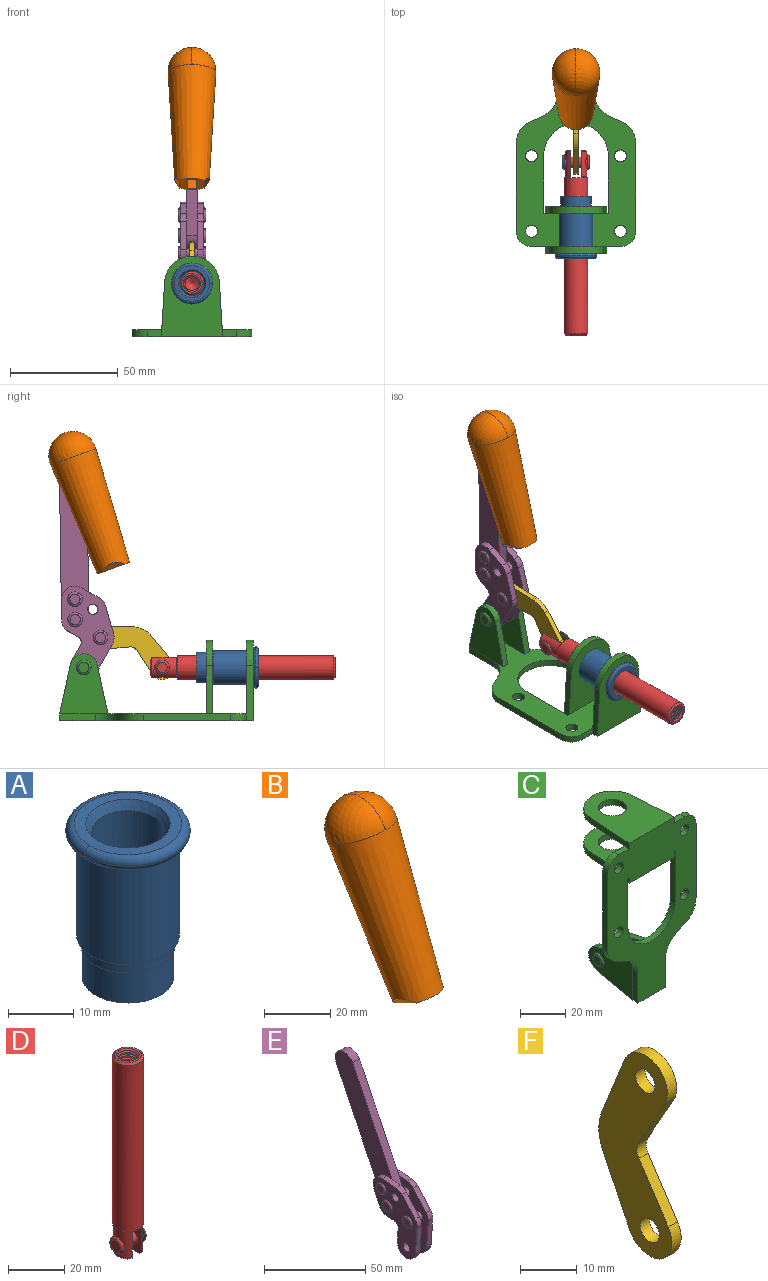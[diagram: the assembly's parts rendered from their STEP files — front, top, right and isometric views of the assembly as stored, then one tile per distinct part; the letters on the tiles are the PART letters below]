
ASSEMBLY  parts=6 mates=6
PART A: 15 faces, bbox 20.6x20.6x28.7 mm
  f0: torus R=8.26mm, axis (0,0,1), area 56.8mm2, adj f1,f10,f12
  f1: torus R=8.26mm, axis (0,0,1), area 56.8mm2, adj f0,f6,f13
  f2: cylinder r=5.59mm len=25.91mm, axis (0,0,1), area 909.6mm2, adj f3,f4
  f3: cone r=6.86mm half-angle=45deg, axis (0,0,-1), area 70.2mm2, adj f2,f14
  f4: cone r=6.47mm half-angle=30deg, axis (0,0,1), area 66.7mm2, adj f2,f13
  f5: cylinder r=7.04mm len=14.07mm, axis (0,0,1), area 252.6mm2, adj f11,f14
  f6: torus R=8.26mm, axis (0,0,1), area 56.8mm2, adj f1,f12,f13
  f7: cylinder r=7.16mm len=14.33mm, axis (0,0,1), area 91.5mm2, adj f9,f11
  f8: cylinder r=7.86mm len=18.42mm, axis (0,0,1), area 909.6mm2, adj f9,f10
  f9: plane 15.72x15.72mm, normal (0,0,-1), area 33mm2, adj f7,f8
  f10: plane 16.51x16.51mm, normal (0,0,-1), area 19.9mm2, adj f0,f8,f12
  f11: plane 14.33x14.33mm, normal (0,0,-1), area 5.7mm2, adj f5,f7
  f12: torus R=8.26mm, axis (0,0,1), area 56.8mm2, adj f0,f6,f10
  f13: plane 16.51x16.51mm, normal (0,0,1), area 82.7mm2, adj f1,f4,f6
  f14: plane 14.07x14.07mm, normal (0,0,-1), area 7.8mm2, adj f3,f5
PART B: 11 faces, bbox 22.3x42.6x64.5 mm
  f0: sphere r=11.13mm, area 411.4mm2, adj f1,f8
  f1: cone r=11.11mm half-angle=3.3deg, axis (0,0.44,0.9), area 3251.8mm2, adj f0,f7,f8,f9,f10
  f2: cylinder r=6.16mm len=11.7mm, axis (1,0,0), area 89.5mm2, adj f3,f4,f5,f6
  f3: plane 60.23x36.75mm, normal (-1,0,0), area 763.6mm2, adj f2,f4,f6,f10
  f4: plane 51.37x25.05mm, normal (0,0.9,-0.44), area 264.2mm2, adj f2,f3,f5,f10
  f5: plane 60.23x36.75mm, normal (1,0,0), area 763.6mm2, adj f2,f4,f6,f10
  f6: plane 51.37x25.05mm, normal (0,-0.9,0.44), area 264.2mm2, adj f2,f3,f5,f10
  f7: plane 9.95x5.95mm, normal (0.71,-0.31,-0.64), area 25.8mm2, adj f1,f10
  f8: sphere r=11.13mm, area 411.4mm2, adj f0,f1
  f9: plane 9.95x5.95mm, normal (-0.71,-0.31,-0.64), area 25.8mm2, adj f1,f10
  f10: plane 14.27x11.38mm, normal (0,-0.44,-0.9), area 106.7mm2, adj f1,f3,f4,f5,f6,f7,f9
PART C: 55 faces, bbox 55.7x37.4x89.8 mm
  f0: torus R=2.41mm, axis (-1,0,0), area 15mm2, adj f11,f15,f25
  f1: torus R=2.41mm, axis (-1,0,0), area 15mm2, adj f10,f12,f22
  f2: cylinder r=2.78mm len=5.56mm, axis (0,-1,0), area 54.2mm2, adj f30,f54
  f3: cylinder r=14.99mm len=29.97mm, axis (0,-1,0), area 145.9mm2, adj f30,f49,f53,f54
  f4: cylinder r=2.78mm len=5.56mm, axis (0,-1,0), area 54.2mm2, adj f30,f54
  f5: cylinder r=2.78mm len=5.56mm, axis (0,-1,0), area 54.2mm2, adj f30,f54
  f6: cylinder r=2.78mm len=5.56mm, axis (0,-1,0), area 54.2mm2, adj f30,f54
  f7: cylinder r=6.35mm len=12.7mm, axis (0,0,1), area 123.6mm2, adj f27,f51
  f8: cylinder r=6.35mm len=12.7mm, axis (0,0,-1), area 124.7mm2, adj f21,f35
  f9: cylinder r=2.41mm len=11.18mm, axis (-1,0,0), area 169.4mm2, adj f16,f19
  f10: plane 4.83x4.83mm, normal (1,0,0), area 18.3mm2, adj f1,f12
  f11: plane 4.83x4.83mm, normal (-1,0,0), area 18.3mm2, adj f0,f15
  f12: torus R=2.41mm, axis (-1,0,0), area 15mm2, adj f1,f10,f22
  f13: cylinder r=6.35mm len=12.41mm, axis (1,0,0), area 53.4mm2, adj f18,f19,f22,f23
  f14: cylinder r=6.35mm len=12.41mm, axis (-1,0,0), area 53.4mm2, adj f16,f17,f24,f25
  f15: torus R=2.41mm, axis (-1,0,0), area 15mm2, adj f0,f11,f25
  f16: plane 27.86x22.35mm, normal (1,0,0), area 425.4mm2, adj f9,f14,f17,f24,f30
  f17: plane 22.86x4.97mm, normal (0,0.21,0.98), area 72.5mm2, adj f14,f16,f25,f30
  f18: plane 22.86x4.97mm, normal (0,0.21,0.98), area 72.5mm2, adj f13,f19,f22,f30
  f19: plane 27.86x22.35mm, normal (-1,0,0), area 425.4mm2, adj f9,f13,f18,f23,f30
  f20: cylinder r=12.7mm len=25.35mm, axis (0,0,-1), area 119.8mm2, adj f21,f34,f35,f36
  f21: plane 34.21x28.07mm, normal (0,0,-1), area 702.4mm2, adj f8,f20,f30,f34,f36
  f22: plane 27.96x22.45mm, normal (1,0,0), area 407.2mm2, adj f1,f12,f13,f18,f23,f30,f42,f43
  f23: plane 22.86x4.97mm, normal (0,0.21,-0.98), area 72.5mm2, adj f13,f19,f22,f44
  f24: plane 22.86x4.97mm, normal (0,0.21,-0.98), area 72.5mm2, adj f14,f16,f25,f44
  f25: plane 27.86x22.35mm, normal (-1,0,0), area 407.1mm2, adj f0,f14,f15,f17,f24,f30,f45,f46
  f26: plane 3.1x0.95mm, normal (0,0,-1), area 2.7mm2, adj f30,f49,f50,f54
  f27: plane 34.21x28.07mm, normal (0,0,1), area 702.4mm2, adj f7,f28,f30,f50,f52
  f28: cylinder r=12.7mm len=25.35mm, axis (0,0,1), area 118.8mm2, adj f27,f50,f51,f52
  f29: plane 3.1x0.95mm, normal (0,0,-1), area 2.7mm2, adj f30,f52,f53,f54
  f30: plane 86.54x55.63mm, normal (0,1,0), area 2362.9mm2, adj f2,f3,f4,f5,f6,f16,f17,f18
  f31: plane 40.56x3.1mm, normal (-1,0,0), area 125.7mm2, adj f30,f32,f48,f54
  f32: cylinder r=7.11mm len=7.11mm, axis (0,-1,0), area 34.6mm2, adj f30,f31,f33,f54
  f33: plane 6.67x3.1mm, normal (0,0,1), area 20.4mm2, adj f30,f32,f34,f54
  f34: plane 25.39x3.13mm, normal (-1,0.06,0), area 79.5mm2, adj f20,f21,f33,f35,f54
  f35: plane 37.31x28.45mm, normal (0,0,1), area 789.9mm2, adj f8,f20,f34,f36,f54
  f36: plane 25.39x3.13mm, normal (1,0.06,0), area 79.5mm2, adj f20,f21,f35,f37,f54
  f37: plane 6.67x3.1mm, normal (0,0,1), area 20.4mm2, adj f30,f36,f38,f54
  f38: cylinder r=7.11mm len=7.11mm, axis (0,-1,0), area 34.6mm2, adj f30,f37,f39,f54
  f39: plane 40.56x3.1mm, normal (1,0,0), area 125.7mm2, adj f30,f38,f40,f54
  f40: cylinder r=11.18mm len=10.16mm, axis (0,-1,0), area 39.5mm2, adj f30,f39,f41,f54
  f41: plane 6.09x3.1mm, normal (0.42,0,-0.91), area 20.8mm2, adj f30,f40,f42,f54
  f42: cylinder r=11.18mm len=9.41mm, axis (0,-1,0), area 37.2mm2, adj f22,f30,f41,f43,f54
  f43: plane 16.5x3.1mm, normal (1,0,0), area 51.1mm2, adj f22,f42,f44,f54
  f44: plane 17.37x3.1mm, normal (0,0,-1), area 53.8mm2, adj f23,f24,f30,f43,f45,f54
  f45: plane 16.5x3.1mm, normal (-1,0,0), area 51.1mm2, adj f25,f44,f46,f54
  f46: cylinder r=11.18mm len=9.41mm, axis (0,-1,0), area 37.2mm2, adj f25,f30,f45,f47,f54
  f47: plane 6.09x3.1mm, normal (-0.42,0,-0.91), area 20.8mm2, adj f30,f46,f48,f54
  f48: cylinder r=11.18mm len=10.16mm, axis (0,-1,0), area 39.5mm2, adj f30,f31,f47,f54
  f49: plane 26.54x3.1mm, normal (-1,0,0), area 82.3mm2, adj f3,f26,f30,f54
  f50: plane 25.39x3.1mm, normal (1,0.06,0), area 78.8mm2, adj f26,f27,f28,f51,f54
  f51: plane 37.31x28.45mm, normal (0,0,-1), area 789.9mm2, adj f7,f28,f50,f52,f54
  f52: plane 25.39x3.1mm, normal (-1,0.06,0), area 78.8mm2, adj f27,f28,f29,f51,f54
  f53: plane 26.54x3.1mm, normal (1,0,0), area 82.3mm2, adj f3,f29,f30,f54
  f54: plane 89.66x55.63mm, normal (0,-1,0), area 2678.5mm2, adj f2,f3,f4,f5,f6,f26,f29,f31
PART D: 48 faces, bbox 12.6x11.1x86.1 mm
  f0: torus R=2.41mm, axis (-1,0,0), area 15mm2, adj f30,f32,f34
  f1: torus R=2.41mm, axis (-1,0,0), area 15mm2, adj f29,f31,f33
  f2: cylinder r=5.54mm len=72.39mm, axis (0,0,1), area 2518.5mm2, adj f3,f4,f42,f43
  f3: cone r=5.54mm half-angle=45deg, axis (0,0,1), area 7.6mm2, adj f2,f5,f41
  f4: cone r=5.54mm half-angle=45deg, axis (0,0,-1), area 34.9mm2, adj f2,f39
  f5: cylinder r=5.08mm len=11.48mm, axis (0,0,1), area 108.3mm2, adj f3,f7,f8,f41
  f6: cylinder r=2.41mm len=4.83mm, axis (-1,0,0), area 71.2mm2, adj f40,f41
  f7: cylinder r=2.41mm len=4.83mm, axis (-1,0,0), area 7.6mm2, adj f5,f34
  f8: cone r=5.08mm half-angle=45deg, axis (0,0,1), area 10.6mm2, adj f5,f37,f41
  f9: cone r=3.98mm half-angle=45deg, axis (0,0,1), area 17.6mm2, adj f27,f39,f45,f46,f47
  f10: cylinder r=2.41mm len=4.83mm, axis (-1,0,0), area 7.6mm2, adj f33,f38
  f11: cylinder r=3.2mm len=6.4mm, axis (0,0,1), area 78.4mm2, adj f12,f28,f44,f45,f47
  f12: cylinder r=3.2mm len=6.4mm, axis (0,0,1), area 10.5mm2, adj f11,f13,f45,f47
  f13: cylinder r=3.2mm len=6.4mm, axis (0,0,1), area 10.5mm2, adj f12,f14,f45,f47
  f14: cylinder r=3.2mm len=6.4mm, axis (0,0,1), area 10.5mm2, adj f13,f15,f45,f47
  f15: cylinder r=3.2mm len=6.4mm, axis (0,0,1), area 10.5mm2, adj f14,f16,f45,f47
  f16: cylinder r=3.2mm len=6.4mm, axis (0,0,1), area 10.5mm2, adj f15,f17,f45,f47
  f17: cylinder r=3.2mm len=6.4mm, axis (0,0,1), area 10.5mm2, adj f16,f18,f45,f47
  f18: cylinder r=3.2mm len=6.4mm, axis (0,0,1), area 10.5mm2, adj f17,f19,f45,f47
  f19: cylinder r=3.2mm len=6.4mm, axis (0,0,1), area 10.5mm2, adj f18,f20,f45,f47
  f20: cylinder r=3.2mm len=6.4mm, axis (0,0,1), area 10.5mm2, adj f19,f21,f45,f47
  f21: cylinder r=3.2mm len=6.4mm, axis (0,0,1), area 10.5mm2, adj f20,f22,f45,f47
  f22: cylinder r=3.2mm len=6.4mm, axis (0,0,1), area 10.5mm2, adj f21,f23,f45,f47
  f23: cylinder r=3.2mm len=6.4mm, axis (0,0,1), area 10.5mm2, adj f22,f24,f45,f47
  f24: cylinder r=3.2mm len=6.4mm, axis (0,0,1), area 10.5mm2, adj f23,f25,f45,f47
  f25: cylinder r=3.2mm len=6.4mm, axis (0,0,1), area 10.5mm2, adj f24,f26,f45,f47
  f26: cylinder r=3.2mm len=6.4mm, axis (0,0,1), area 10.5mm2, adj f25,f27,f45,f47
  f27: cylinder r=3.2mm len=6.4mm, axis (0,0,1), area 7.4mm2, adj f9,f26,f45,f47
  f28: cone r=3.2mm half-angle=60deg, axis (0,0,1), area 37.2mm2, adj f11
  f29: plane 4.83x4.83mm, normal (-1,0,0), area 18.3mm2, adj f1,f31
  f30: plane 4.83x4.83mm, normal (1,0,0), area 18.3mm2, adj f0,f32
  f31: torus R=2.41mm, axis (-1,0,0), area 15mm2, adj f1,f29,f33
  f32: torus R=2.41mm, axis (-1,0,0), area 15mm2, adj f0,f30,f34
  f33: plane 6.83x6.83mm, normal (1,0,0), area 18.3mm2, adj f1,f10,f31
  f34: plane 6.83x6.83mm, normal (-1,0,0), area 18.3mm2, adj f0,f7,f32
  f35: cone r=5.08mm half-angle=45deg, axis (0,0,1), area 10.6mm2, adj f36,f38,f40
  f36: plane 7.25x1.97mm, normal (0,0,-1), area 10mm2, adj f35,f40
  f37: plane 7.25x1.97mm, normal (0,0,-1), area 10mm2, adj f8,f41
  f38: cylinder r=5.08mm len=11.48mm, axis (0,0,1), area 108.3mm2, adj f10,f35,f40,f42
  f39: plane 9.55x9.55mm, normal (0,0,1), area 22mm2, adj f4,f9
  f40: plane 12.76x10.09mm, normal (1,0,0), area 95.7mm2, adj f6,f35,f36,f38,f42,f43
  f41: plane 12.76x10.09mm, normal (-1,0,0), area 95.7mm2, adj f3,f5,f6,f8,f37,f43
  f42: cone r=5.54mm half-angle=45deg, axis (0,0,1), area 7.6mm2, adj f2,f38,f40
  f43: plane 11.07x4.7mm, normal (0,0,-1), area 50.4mm2, adj f2,f40,f41
  f44: plane 0.89x0.62mm, normal (-1,0,0), area 0.3mm2, adj f11,f45,f46,f47
  f45: bspline ~24.8x7.63mm, area 266.6mm2, adj f9,f11,f12,f13,f14,f15,f16,f17
  f46: bspline ~24.87x7.63mm, area 73.6mm2, adj f9,f44,f45,f47
  f47: bspline ~24.98x7.63mm, area 272.5mm2, adj f9,f11,f12,f13,f14,f15,f16,f17
PART E: 59 faces, bbox 12.9x60.2x99.6 mm
  f0: torus R=2.39mm, axis (-1,0,0), area 14.9mm2, adj f20,f43,f51
  f1: torus R=2.39mm, axis (-1,0,0), area 14.9mm2, adj f19,f42,f51
  f2: torus R=2.39mm, axis (-1,0,0), area 14.9mm2, adj f18,f35,f51
  f3: torus R=2.39mm, axis (-1,0,0), area 14.9mm2, adj f14,f17,f23
  f4: torus R=2.39mm, axis (-1,0,0), area 14.9mm2, adj f13,f16,f23
  f5: torus R=2.39mm, axis (-1,0,0), area 14.9mm2, adj f12,f15,f23
  f6: cylinder r=2.39mm len=4.78mm, axis (1,0,0), area 46.5mm2, adj f48,f50,f51
  f7: cylinder r=2.39mm len=4.78mm, axis (1,0,0), area 46.5mm2, adj f50,f51
  f8: cylinder r=6.35mm len=12.68mm, axis (1,0,0), area 61.8mm2, adj f38,f39,f50,f51
  f9: cylinder r=2.39mm len=4.78mm, axis (-1,0,0), area 70.5mm2, adj f46,f50
  f10: cylinder r=2.39mm len=4.78mm, axis (-1,0,0), area 46.5mm2, adj f23,f45,f46
  f11: cylinder r=2.39mm len=4.78mm, axis (-1,0,0), area 46.5mm2, adj f23,f46
  f12: plane 4.78x4.78mm, normal (1,0,0), area 17.9mm2, adj f5,f15
  f13: plane 4.78x4.78mm, normal (1,0,0), area 17.9mm2, adj f4,f16
  f14: plane 4.78x4.78mm, normal (1,0,0), area 17.9mm2, adj f3,f17
  f15: torus R=2.39mm, axis (-1,0,0), area 14.9mm2, adj f5,f12,f23
  f16: torus R=2.39mm, axis (-1,0,0), area 14.9mm2, adj f4,f13,f23
  f17: torus R=2.39mm, axis (-1,0,0), area 14.9mm2, adj f3,f14,f23
  f18: plane 4.78x4.78mm, normal (-1,0,0), area 17.9mm2, adj f2,f35
  f19: plane 4.78x4.78mm, normal (-1,0,0), area 17.9mm2, adj f1,f42
  f20: plane 4.78x4.78mm, normal (-1,0,0), area 17.9mm2, adj f0,f43
  f21: plane 2.26x0.2mm, normal (1,0,0), area 0.2mm2, adj f31,f44
  f22: plane 2.26x0.2mm, normal (-1,0,0), area 0.2mm2, adj f41,f44
  f23: plane 39.37x30.77mm, normal (1,0,0), area 565.5mm2, adj f3,f4,f5,f10,f11,f15,f16,f17
  f24: cylinder r=6.1mm len=4.15mm, axis (-1,0,0), area 14.7mm2, adj f23,f25,f32,f46
  f25: plane 10.25x9.01mm, normal (0,-0.75,0.66), area 42.3mm2, adj f23,f24,f26,f46
  f26: cylinder r=6.35mm len=4.64mm, axis (-1,0,0), area 15.6mm2, adj f23,f25,f27,f46
  f27: plane 15.84x3.1mm, normal (0,-1,-0.07), area 49.2mm2, adj f23,f26,f28,f46
  f28: cylinder r=6.35mm len=12.68mm, axis (-1,0,0), area 61.8mm2, adj f23,f27,f29,f46
  f29: plane 8.11x3.1mm, normal (0,1,0.07), area 25.2mm2, adj f23,f28,f30,f46
  f30: cylinder r=3.05mm len=3.25mm, axis (-1,0,0), area 14.8mm2, adj f23,f29,f31,f46
  f31: plane 5.99x3.1mm, normal (0,0.07,-1), area 18.6mm2, adj f21,f23,f30,f44,f46
  f32: plane 9.5x3.1mm, normal (0,-0.07,1), area 29.5mm2, adj f23,f24,f33,f46,f47
  f33: cylinder r=6.1mm len=8.63mm, axis (-1,0,0), area 39.1mm2, adj f23,f32,f34,f47
  f34: plane 8.65x3.96mm, normal (0,0.91,-0.42), area 29.5mm2, adj f23,f33,f44,f47
  f35: torus R=2.39mm, axis (-1,0,0), area 14.9mm2, adj f2,f18,f51
  f36: plane 10.25x9.01mm, normal (0,-0.75,0.66), area 42.3mm2, adj f37,f49,f50,f51
  f37: cylinder r=6.35mm len=4.64mm, axis (1,0,0), area 15.6mm2, adj f36,f38,f50,f51
  f38: plane 15.84x3.1mm, normal (0,-1,-0.07), area 49.2mm2, adj f8,f37,f50,f51
  f39: plane 8.11x3.1mm, normal (0,1,0.07), area 25.2mm2, adj f8,f40,f50,f51
  f40: cylinder r=3.05mm len=3.25mm, axis (1,0,0), area 14.8mm2, adj f39,f41,f50,f51
  f41: plane 5.99x3.1mm, normal (0,0.07,-1), area 18.6mm2, adj f22,f40,f44,f50,f51
  f42: torus R=2.39mm, axis (-1,0,0), area 14.9mm2, adj f1,f19,f51
  f43: torus R=2.39mm, axis (-1,0,0), area 14.9mm2, adj f0,f20,f51
  f44: cylinder r=6.35mm len=12.12mm, axis (-1,0,0), area 128.9mm2, adj f21,f22,f23,f31,f34,f41,f46,f47
  f45: plane 2.65x1.35mm, normal (1,0,0), area 1mm2, adj f10,f55
  f46: plane 39.08x20.42mm, normal (-1,0,0), area 412.5mm2, adj f9,f10,f11,f24,f25,f26,f27,f28
  f47: plane 77.62x39.82mm, normal (1,0,0), area 850mm2, adj f32,f33,f34,f44,f53,f54,f55
  f48: plane 2.65x1.35mm, normal (-1,0,0), area 1mm2, adj f6,f55
  f49: cylinder r=6.1mm len=4.15mm, axis (1,0,0), area 14.7mm2, adj f36,f50,f51,f56
  f50: plane 39.08x20.42mm, normal (1,0,0), area 412.5mm2, adj f6,f7,f8,f9,f36,f37,f38,f39
  f51: plane 39.37x30.77mm, normal (-1,0,0), area 565.5mm2, adj f0,f1,f2,f6,f7,f8,f35,f36
  f52: plane 8.65x3.96mm, normal (0,0.91,-0.42), area 29.5mm2, adj f44,f51,f57,f58
  f53: plane 68.49x33.4mm, normal (0,0.9,-0.44), area 358.1mm2, adj f44,f47,f54,f58
  f54: cylinder r=6.35mm len=12.06mm, axis (1,0,0), area 93.7mm2, adj f47,f53,f55,f58
  f55: plane 68.49x33.4mm, normal (0,-0.9,0.44), area 358.1mm2, adj f44,f45,f46,f47,f48,f50,f54,f58
  f56: plane 9.5x3.1mm, normal (0,-0.07,1), area 29.5mm2, adj f49,f50,f51,f57,f58
  f57: cylinder r=6.1mm len=8.63mm, axis (1,0,0), area 39.1mm2, adj f51,f52,f56,f58
  f58: plane 77.62x39.82mm, normal (-1,0,0), area 850mm2, adj f44,f52,f53,f54,f55,f56,f57
PART F: 12 faces, bbox 2.3x18.2x42.8 mm
  f0: cylinder r=2.4mm len=4.8mm, axis (1,0,0), area 34.9mm2, adj f4,f11
  f1: cylinder r=10.41mm len=8.47mm, axis (1,0,0), area 20.2mm2, adj f4,f9,f10,f11
  f2: cylinder r=3.05mm len=3.16mm, axis (1,0,0), area 7.7mm2, adj f4,f6,f7,f11
  f3: cylinder r=2.4mm len=4.8mm, axis (1,0,0), area 34.9mm2, adj f4,f11
  f4: plane 42.81x18.23mm, normal (-1,0,0), area 414.1mm2, adj f0,f1,f2,f3,f5,f6,f7,f8
  f5: cylinder r=5.54mm len=10.67mm, axis (1,0,0), area 41.8mm2, adj f4,f6,f10,f11
  f6: plane 11.66x6.53mm, normal (0,-0.87,-0.49), area 30.9mm2, adj f2,f4,f5,f11
  f7: plane 11.17x7.33mm, normal (0,-0.84,0.55), area 30.9mm2, adj f2,f4,f8,f11
  f8: cylinder r=5.54mm len=10.51mm, axis (1,0,0), area 41.8mm2, adj f4,f7,f9,f11
  f9: plane 13.67x6.67mm, normal (0,0.9,-0.44), area 35.1mm2, adj f1,f4,f8,f11
  f10: plane 14.1x5.7mm, normal (0,0.93,0.37), area 35.1mm2, adj f1,f4,f5,f11
  f11: plane 42.81x18.23mm, normal (1,0,0), area 414.1mm2, adj f0,f1,f2,f3,f5,f6,f7,f8
PLACE A rot(axis=(0,-0.71,0.71),180deg) t=(0,9.14,49.23)mm
PLACE B rot(axis=(1,0,0),6.2deg) t=(0,-17.89,62.39)mm
PLACE C rot(axis=(1,0,0),90deg) t=(0,9.14,0)mm fixed
PLACE D rot(axis=(1,0,0),90deg) t=(0,20.4,0)mm
PLACE E rot(axis=(1,0,0),25.2deg) t=(0,5.31,43.19)mm
PLACE F rot(axis=(1,0,0),117.9deg) t=(0,30.12,10.09)mm
MATE revolute D.f6 <-> F.f5  axis (-1,0,0) through (0,4.93,24.61)mm
MATE slider D.f2 <-> A.f2  axis (0,-1,0) through (0,-38.38,24.61)mm
MATE revolute E.f7 <-> C.f0  axis (-1,0,0) through (0,41.23,24.61)mm
MATE fastened E.f54 <-> B.f0  axis (1,0,0) through (0,46.3,122.98)mm
MATE revolute F.f3 <-> E.f4  axis (1,0,0) through (0,33.49,38.47)mm
MATE fastened C.f7 <-> A.f2  axis (0,-1,0) through (0,-37.25,24.61)mm
